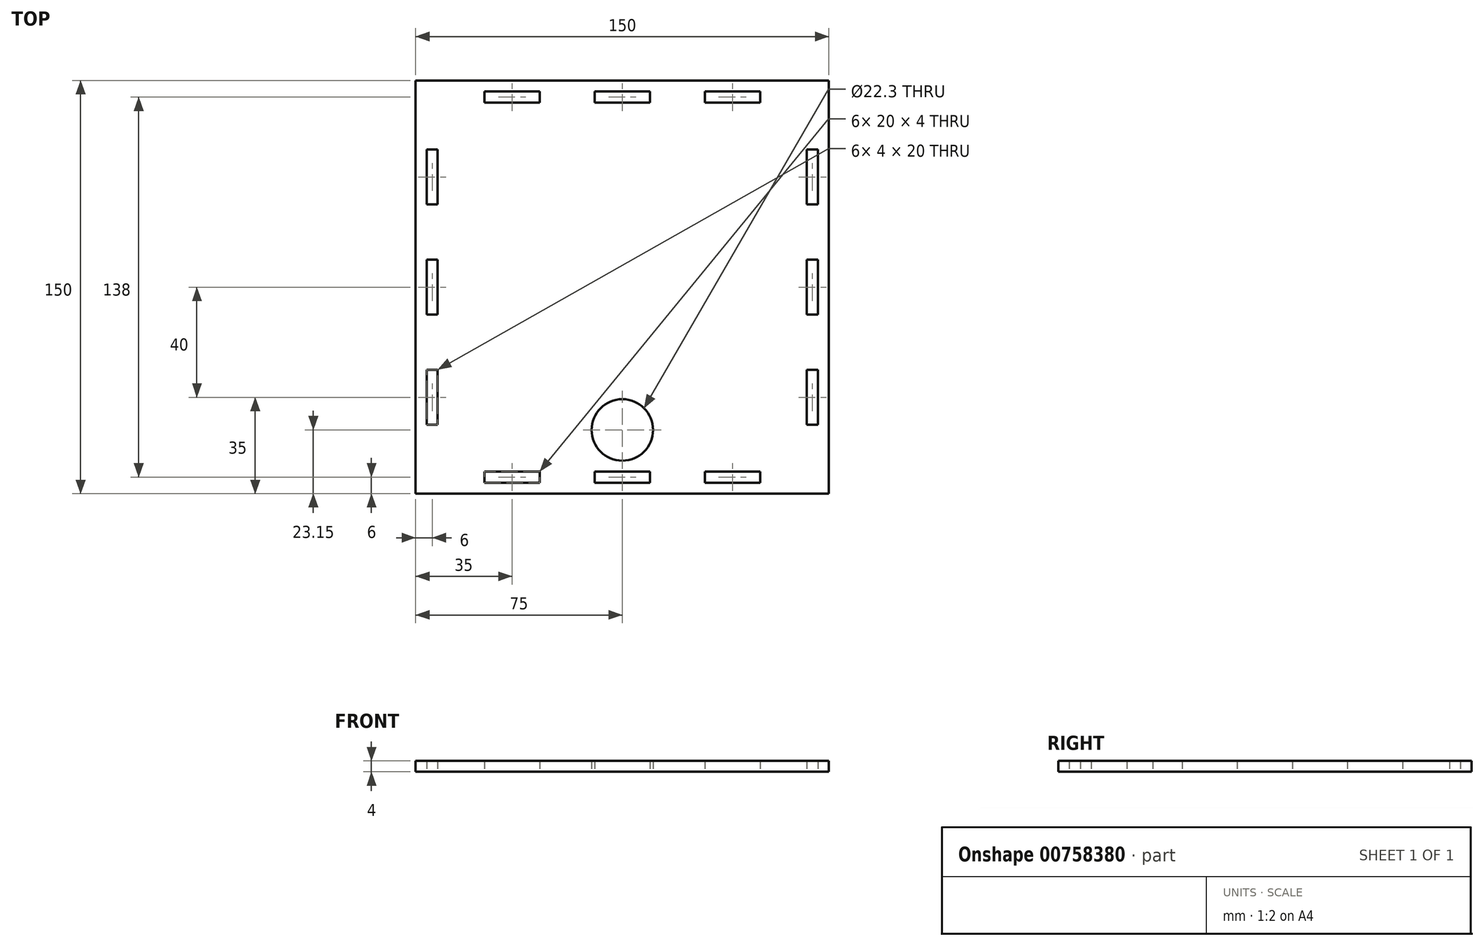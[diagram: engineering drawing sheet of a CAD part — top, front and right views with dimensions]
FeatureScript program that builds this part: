
annotation { "Feature Type Name" : "Feature", "Feature Type Description" : "" }
export const myFeature = defineFeature(function(context is Context, id is Id, definition is map)
    precondition{}
    {
        {
            var Q0;
            Q0=qCreatedBy(makeId("Top.planeOp"),FACE);
            var sketch = newSketch(context, id + "F0", { "sketchPlane" : qUnion([Q0])});
            skLineSegment(sketch, "E0.bottom", {"start": v(75, 75) * mm, "end": v(-75, 75) * mm});
            skLineSegment(sketch, "E0.top", {"start": v(75, -75) * mm, "end": v(-75, -75) * mm});
            skLineSegment(sketch, "E0.left", {"start": v(75, 75) * mm, "end": v(75, -75) * mm});
            skLineSegment(sketch, "E0.right", {"start": v(-75, 75) * mm, "end": v(-75, -75) * mm});
            skPoint(sketch, "E0.middle", {"position": v(0, 0) * mm});
            skLineSegment(sketch, "E1", {"start": v(0, 71) * mm, "end": v(10, 71) * mm});
            skLineSegment(sketch, "E2", {"start": v(10, 71) * mm, "end": v(10, 67) * mm});
            skLineSegment(sketch, "E3", {"start": v(10, 67) * mm, "end": v(0, 67) * mm});
            skLineSegment(sketch, "E4.MirrorCS", {"start": v(-10, 67) * mm, "end": v(0, 67) * mm});
            skLineSegment(sketch, "E5.MirrorCS", {"start": v(0, 71) * mm, "end": v(-10, 71) * mm});
            skLineSegment(sketch, "E6.MirrorCS", {"start": v(-10, 71) * mm, "end": v(-10, 67) * mm});
            skLineSegment(sketch, "E7.1.0.0", {"start": v(40, 71) * mm, "end": v(30, 71) * mm});
            skLineSegment(sketch, "E7.1.0.1", {"start": v(30, 67) * mm, "end": v(40, 67) * mm});
            skLineSegment(sketch, "E7.1.0.2", {"start": v(40, 71) * mm, "end": v(50, 71) * mm});
            skLineSegment(sketch, "E7.1.0.3", {"start": v(50, 67) * mm, "end": v(40, 67) * mm});
            skLineSegment(sketch, "E7.1.0.4", {"start": v(50, 71) * mm, "end": v(50, 67) * mm});
            skLineSegment(sketch, "E7.1.0.5", {"start": v(30, 71) * mm, "end": v(30, 67) * mm});
            skLineSegment(sketch, "E8.MirrorCS", {"start": v(-30, 67) * mm, "end": v(-40, 67) * mm});
            skLineSegment(sketch, "E9.MirrorCS", {"start": v(-30, 71) * mm, "end": v(-30, 67) * mm});
            skLineSegment(sketch, "E10.MirrorCS", {"start": v(-40, 71) * mm, "end": v(-30, 71) * mm});
            skLineSegment(sketch, "E11.MirrorCS", {"start": v(-50, 67) * mm, "end": v(-40, 67) * mm});
            skLineSegment(sketch, "E12.MirrorCS", {"start": v(-40, 71) * mm, "end": v(-50, 71) * mm});
            skLineSegment(sketch, "E13.MirrorCS", {"start": v(-50, 71) * mm, "end": v(-50, 67) * mm});
            skLineSegment(sketch, "E14.MirrorCS", {"start": v(-10, -67) * mm, "end": v(0, -67) * mm});
            skLineSegment(sketch, "E15.MirrorCS", {"start": v(10, -67) * mm, "end": v(0, -67) * mm});
            skLineSegment(sketch, "E16.MirrorCS", {"start": v(0, -71) * mm, "end": v(-10, -71) * mm});
            skLineSegment(sketch, "E17.MirrorCS", {"start": v(0, -71) * mm, "end": v(10, -71) * mm});
            skLineSegment(sketch, "E18.MirrorCS", {"start": v(-40, -71) * mm, "end": v(-30, -71) * mm});
            skLineSegment(sketch, "E19.MirrorCS", {"start": v(-40, -71) * mm, "end": v(-50, -71) * mm});
            skLineSegment(sketch, "E20.MirrorCS", {"start": v(-50, -67) * mm, "end": v(-40, -67) * mm});
            skLineSegment(sketch, "E21.MirrorCS", {"start": v(-30, -67) * mm, "end": v(-40, -67) * mm});
            skLineSegment(sketch, "E22.MirrorCS", {"start": v(40, -71) * mm, "end": v(30, -71) * mm});
            skLineSegment(sketch, "E23.MirrorCS", {"start": v(40, -71) * mm, "end": v(50, -71) * mm});
            skLineSegment(sketch, "E24.MirrorCS", {"start": v(50, -67) * mm, "end": v(40, -67) * mm});
            skLineSegment(sketch, "E25.MirrorCS", {"start": v(30, -67) * mm, "end": v(40, -67) * mm});
            skLineSegment(sketch, "E26.MirrorCS", {"start": v(50, -71) * mm, "end": v(50, -67) * mm});
            skLineSegment(sketch, "E27.MirrorCS", {"start": v(30, -71) * mm, "end": v(30, -67) * mm});
            skLineSegment(sketch, "E28.MirrorCS", {"start": v(10, -71) * mm, "end": v(10, -67) * mm});
            skLineSegment(sketch, "E29.MirrorCS", {"start": v(-10, -71) * mm, "end": v(-10, -67) * mm});
            skLineSegment(sketch, "E30.MirrorCS", {"start": v(-50, -71) * mm, "end": v(-50, -67) * mm});
            skLineSegment(sketch, "E31.MirrorCS", {"start": v(-30, -71) * mm, "end": v(-30, -67) * mm});
            skLineSegment(sketch, "E32", {"start": v(-71, 0) * mm, "end": v(-71, 10) * mm});
            skLineSegment(sketch, "E33", {"start": v(-71, 10) * mm, "end": v(-67, 10) * mm});
            skLineSegment(sketch, "E34", {"start": v(-67, 10) * mm, "end": v(-67, -10) * mm});
            skLineSegment(sketch, "E35", {"start": v(-67, -10) * mm, "end": v(-71, -10) * mm});
            skLineSegment(sketch, "E36", {"start": v(-71, -10) * mm, "end": v(-71, 0) * mm});
            skLineSegment(sketch, "E37.0.1.0", {"start": v(-67, 50) * mm, "end": v(-67, 30) * mm});
            skLineSegment(sketch, "E37.0.1.1", {"start": v(-71, 40) * mm, "end": v(-71, 50) * mm});
            skLineSegment(sketch, "E37.0.1.2", {"start": v(-71, 30) * mm, "end": v(-71, 40) * mm});
            skLineSegment(sketch, "E37.0.1.3", {"start": v(-67, 30) * mm, "end": v(-71, 30) * mm});
            skLineSegment(sketch, "E37.0.1.4", {"start": v(-71, 50) * mm, "end": v(-67, 50) * mm});
            skLineSegment(sketch, "E37.1.1.0", {"start": v(-67, 50) * mm, "end": v(-67, 30) * mm});
            skLineSegment(sketch, "E37.1.1.1", {"start": v(-71, 40) * mm, "end": v(-71, 50) * mm});
            skLineSegment(sketch, "E37.1.1.2", {"start": v(-71, 30) * mm, "end": v(-71, 40) * mm});
            skLineSegment(sketch, "E37.1.1.3", {"start": v(-67, 30) * mm, "end": v(-71, 30) * mm});
            skLineSegment(sketch, "E37.1.1.4", {"start": v(-71, 50) * mm, "end": v(-67, 50) * mm});
            skLineSegment(sketch, "E37.2.0.0", {"start": v(-67, 0) * mm, "end": v(-67, 0) * mm});
            skLineSegment(sketch, "E37.2.0.2", {"start": v(-71, 0) * mm, "end": v(-71, -10) * mm});
            skLineSegment(sketch, "E37.2.0.3", {"start": v(-67, 0) * mm, "end": v(-71, 0) * mm});
            skLineSegment(sketch, "E37.2.0.4", {"start": v(-71, 0) * mm, "end": v(-67, 0) * mm});
            skLineSegment(sketch, "E37.2.1.0", {"start": v(-67, 50) * mm, "end": v(-67, 30) * mm});
            skLineSegment(sketch, "E37.2.1.1", {"start": v(-71, 40) * mm, "end": v(-71, 50) * mm});
            skLineSegment(sketch, "E37.2.1.2", {"start": v(-71, 30) * mm, "end": v(-71, 40) * mm});
            skLineSegment(sketch, "E37.2.1.3", {"start": v(-67, 30) * mm, "end": v(-71, 30) * mm});
            skLineSegment(sketch, "E37.2.1.4", {"start": v(-71, 50) * mm, "end": v(-67, 50) * mm});
            skLineSegment(sketch, "E37.direction1", {"start": v(-67, -10) * mm, "end": v(-67, -10) * mm});
            skLineSegment(sketch, "E38.MirrorCS", {"start": v(-67, -30) * mm, "end": v(-71, -30) * mm});
            skLineSegment(sketch, "E39.MirrorCS", {"start": v(-71, -30) * mm, "end": v(-71, -40) * mm});
            skLineSegment(sketch, "E40.MirrorCS", {"start": v(-67, -50) * mm, "end": v(-67, -30) * mm});
            skLineSegment(sketch, "E41.MirrorCS", {"start": v(-71, -40) * mm, "end": v(-71, -50) * mm});
            skLineSegment(sketch, "E42.MirrorCS", {"start": v(-71, -50) * mm, "end": v(-67, -50) * mm});
            skLineSegment(sketch, "E43.MirrorCS", {"start": v(67, -50) * mm, "end": v(67, -30) * mm});
            skLineSegment(sketch, "E44.MirrorCS", {"start": v(71, -30) * mm, "end": v(71, -40) * mm});
            skLineSegment(sketch, "E45.MirrorCS", {"start": v(71, -40) * mm, "end": v(71, -50) * mm});
            skLineSegment(sketch, "E46.MirrorCS", {"start": v(71, -50) * mm, "end": v(67, -50) * mm});
            skLineSegment(sketch, "E47.MirrorCS", {"start": v(67, -30) * mm, "end": v(71, -30) * mm});
            skLineSegment(sketch, "E48.MirrorCS", {"start": v(71, -10) * mm, "end": v(71, 0) * mm});
            skLineSegment(sketch, "E49.MirrorCS", {"start": v(71, 0) * mm, "end": v(71, 10) * mm});
            skLineSegment(sketch, "E50.MirrorCS", {"start": v(67, 10) * mm, "end": v(67, -10) * mm});
            skLineSegment(sketch, "E51.MirrorCS", {"start": v(71, 10) * mm, "end": v(67, 10) * mm});
            skLineSegment(sketch, "E52.MirrorCS", {"start": v(67, 30) * mm, "end": v(71, 30) * mm});
            skLineSegment(sketch, "E53.MirrorCS", {"start": v(71, 30) * mm, "end": v(71, 40) * mm});
            skLineSegment(sketch, "E54.MirrorCS", {"start": v(71, 40) * mm, "end": v(71, 50) * mm});
            skLineSegment(sketch, "E55.MirrorCS", {"start": v(71, 50) * mm, "end": v(67, 50) * mm});
            skLineSegment(sketch, "E56.MirrorCS", {"start": v(67, 50) * mm, "end": v(67, 30) * mm});
            skLineSegment(sketch, "E57", {"start": v(67, -10) * mm, "end": v(71, -10) * mm});
            skPoint(sketch, "E58", {"position": v(0, -51.85) * mm});
            skCircle(sketch, "E59", {"center": v(0, -51.85) * mm, "radius": 11.15 * mm});
            skSolve(sketch);
        }
        {
            var Q0;
            Q0=makeQuery(id+"F0.imprint","IMPRINT",FACE,{"disambiguationData":[TD([[makeQuery(id+"F0.imprint","IMPRINT",EDGE,{"derivedFrom":sQuery(id+"F0.wireOp",EDGE,"E0.bottom")}),1.0]])]});
            extrude(context, id + "F1", {"entities" : qUnion([Q0]), "depth" : 4 * mm});
        }
    });
